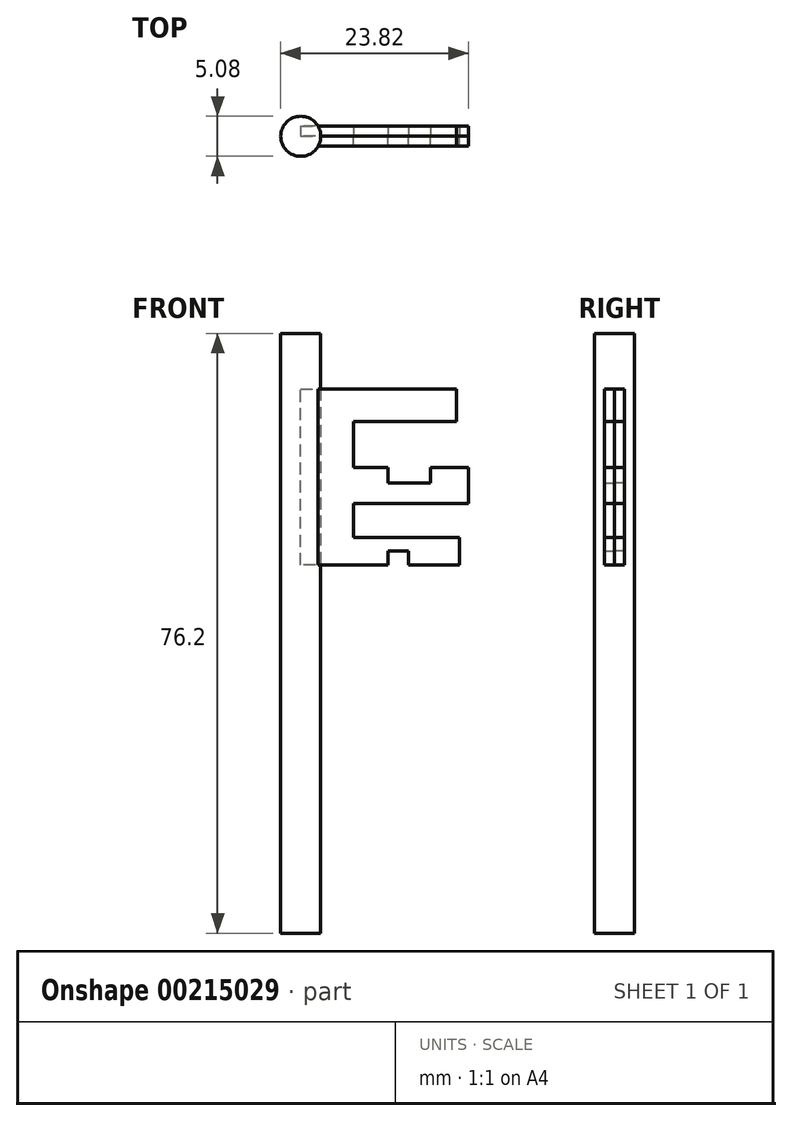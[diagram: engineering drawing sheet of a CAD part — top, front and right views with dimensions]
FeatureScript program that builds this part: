
annotation { "Feature Type Name" : "Feature", "Feature Type Description" : "" }
export const myFeature = defineFeature(function(context is Context, id is Id, definition is map)
    precondition{}
    {
        {
            var Q0;
            Q0=qCreatedBy(makeId("Top.planeOp"),FACE);
            var sketch = newSketch(context, id + "F0", { "sketchPlane" : qUnion([Q0])});
            skCircle(sketch, "E0", {"center": v(0, 0) * mm, "radius": 2.54 * mm});
            skSolve(sketch);
        }
        {
            var Q0;
            Q0 = qSketchRegion(id + "F0", true);
            extrude(context, id + "F1", {"entities" : qUnion([Q0]), "depth" : 76.2 * mm});
        }
        {
            var Q0;
            Q0=qCreatedBy(makeId("Front.planeOp"),FACE);
            var sketch = newSketch(context, id + "F2", { "sketchPlane" : qUnion([Q0])});
            skLineSegment(sketch, "E1", {"start": v(0, 69.15) * mm, "end": v(19.76, 69.15) * mm});
            skLineSegment(sketch, "E2", {"start": v(19.76, 69.15) * mm, "end": v(19.76, 65.03) * mm});
            skLineSegment(sketch, "E3", {"start": v(19.76, 65.03) * mm, "end": v(6.73, 65.03) * mm});
            skLineSegment(sketch, "E4", {"start": v(6.73, 65.03) * mm, "end": v(6.73, 59.17) * mm});
            skLineSegment(sketch, "E5", {"start": v(6.73, 59.17) * mm, "end": v(11.07, 59.17) * mm});
            skLineSegment(sketch, "E6", {"start": v(11.07, 59.17) * mm, "end": v(11.07, 57.21) * mm});
            skLineSegment(sketch, "E7", {"start": v(11.07, 57.21) * mm, "end": v(16.5, 57.21) * mm});
            skLineSegment(sketch, "E8", {"start": v(16.5, 57.21) * mm, "end": v(16.5, 59.17) * mm});
            skLineSegment(sketch, "E9", {"start": v(16.5, 59.17) * mm, "end": v(21.28, 59.17) * mm});
            skLineSegment(sketch, "E10", {"start": v(21.28, 59.17) * mm, "end": v(21.28, 54.6) * mm});
            skLineSegment(sketch, "E11", {"start": v(21.28, 54.6) * mm, "end": v(6.73, 54.6) * mm});
            skLineSegment(sketch, "E12", {"start": v(6.73, 54.6) * mm, "end": v(6.73, 50.26) * mm});
            skLineSegment(sketch, "E13", {"start": v(6.73, 50.26) * mm, "end": v(20.2, 50.26) * mm});
            skLineSegment(sketch, "E14", {"start": v(20.2, 50.26) * mm, "end": v(20.2, 46.8) * mm});
            skLineSegment(sketch, "E15", {"start": v(20.2, 46.8) * mm, "end": v(13.68, 46.8) * mm});
            skLineSegment(sketch, "E16", {"start": v(13.68, 46.8) * mm, "end": v(13.68, 48.53) * mm});
            skLineSegment(sketch, "E17", {"start": v(13.68, 48.53) * mm, "end": v(11.07, 48.53) * mm});
            skLineSegment(sketch, "E18", {"start": v(11.07, 48.53) * mm, "end": v(11.07, 46.8) * mm});
            skLineSegment(sketch, "E19", {"start": v(11.07, 46.8) * mm, "end": v(0, 46.8) * mm});
            skLineSegment(sketch, "E20", {"start": v(0, 46.8) * mm, "end": v(0, 69.15) * mm});
            skSolve(sketch);
        }
        {
            var Q0;
            Q0 = qSketchRegion(id + "F2", true);
            extrude(context, id + "F3", {"entities" : qUnion([Q0]), "operationType" : NewBodyOperationType.ADD, "depth" : 1.27 * mm});
        }
        {
            var Q0;
            Q0 = qSketchRegion(id + "F2", true);
            extrude(context, id + "F4", {"entities" : qUnion([Q0]), "oppositeDirection" : true, "depth" : 1.27 * mm});
        }
    });
